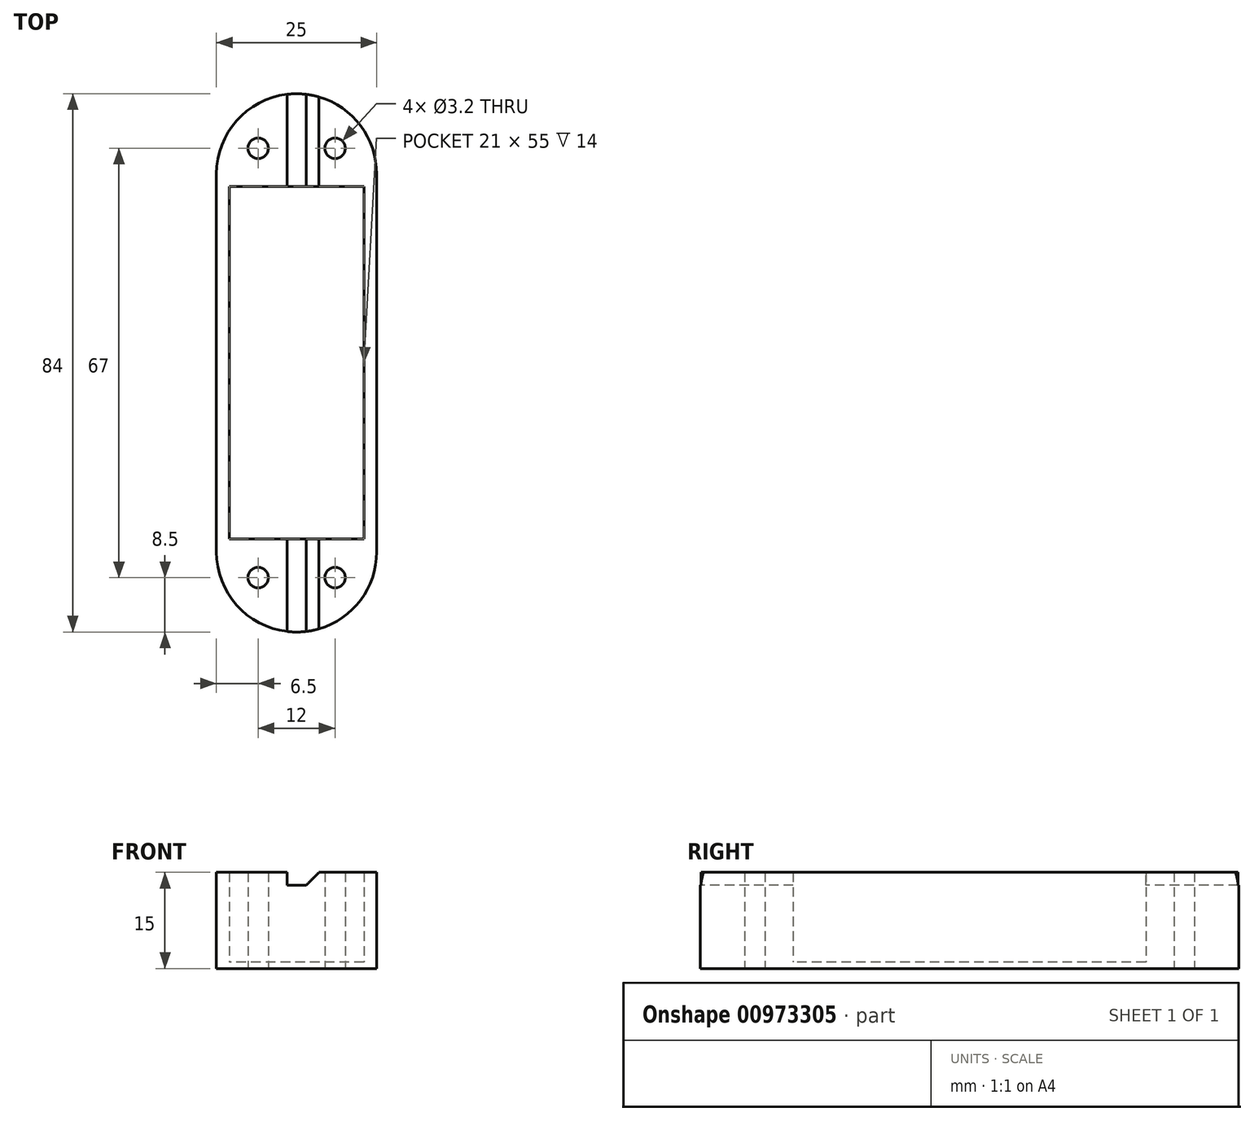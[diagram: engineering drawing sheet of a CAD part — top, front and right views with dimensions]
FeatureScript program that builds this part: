
annotation { "Feature Type Name" : "Feature", "Feature Type Description" : "" }
export const myFeature = defineFeature(function(context is Context, id is Id, definition is map)
    precondition{}
    {
        {
            var Q0;
            Q0=qCreatedBy(makeId("Top.planeOp"),FACE);
            var sketch = newSketch(context, id + "F0", { "sketchPlane" : qUnion([Q0])});
            skLineSegment(sketch, "E0.bottom", {"start": v(10.5, 27.5) * mm, "end": v(-10.5, 27.5) * mm});
            skLineSegment(sketch, "E0.top", {"start": v(10.5, -27.5) * mm, "end": v(-10.5, -27.5) * mm});
            skLineSegment(sketch, "E0.left", {"start": v(10.5, 27.5) * mm, "end": v(10.5, -27.5) * mm});
            skLineSegment(sketch, "E0.right", {"start": v(-10.5, 27.5) * mm, "end": v(-10.5, -27.5) * mm});
            skPoint(sketch, "E0.middle", {"position": v(0, 0) * mm});
            skLineSegment(sketch, "E1.left", {"start": v(12.5, 29.5) * mm, "end": v(12.5, -29.5) * mm});
            skLineSegment(sketch, "E1.right", {"start": v(-12.5, 29.5) * mm, "end": v(-12.5, -29.5) * mm});
            skArc(sketch, "E2", {"start": v(12.5, 29.5) * mm, "mid": v(0, 42) * mm, "end": v(-12.5, 29.5) * mm});
            skArc(sketch, "E3.MirrorCS", {"start": v(12.5, -29.5) * mm, "mid": v(0, -42) * mm, "end": v(-12.5, -29.5) * mm});
            skCircle(sketch, "E4", {"center": v(-6, 33.5) * mm, "radius": 1.6 * mm});
            skCircle(sketch, "E5.MirrorC", {"center": v(6, 33.5) * mm, "radius": 1.6 * mm});
            skCircle(sketch, "E6.MirrorC", {"center": v(-6, -33.5) * mm, "radius": 1.6 * mm});
            skCircle(sketch, "E7.MirrorC", {"center": v(6, -33.5) * mm, "radius": 1.6 * mm});
            skSolve(sketch);
        }
        {
            var Q0;
            Q0=makeQuery(id+"F0.imprint","IMPRINT",FACE,{"disambiguationData":[TD([[makeQuery(id+"F0.imprint","IMPRINT",EDGE,{"derivedFrom":sQuery(id+"F0.wireOp",EDGE,"E0.bottom")}),-1.0]])]});
            extrude(context, id + "F1", {"entities" : qUnion([Q0]), "depth" : 15 * mm, "offsetDistance" : 25 * mm});
        }
        {
            var Q0;
            Q0=qCreatedBy(makeId("Top.planeOp"),FACE);
            var sketch = newSketch(context, id + "F2", { "sketchPlane" : qUnion([Q0])});
            skLineSegment(sketch, "E8.bottom", {"start": v(11.31, -28.6) * mm, "end": v(-11.31, -28.6) * mm});
            skLineSegment(sketch, "E8.top", {"start": v(11.31, 28.6) * mm, "end": v(-11.31, 28.6) * mm});
            skLineSegment(sketch, "E8.left", {"start": v(11.31, -28.6) * mm, "end": v(11.31, 28.6) * mm});
            skLineSegment(sketch, "E8.right", {"start": v(-11.31, -28.6) * mm, "end": v(-11.31, 28.6) * mm});
            skPoint(sketch, "E8.middle", {"position": v(0, 0) * mm});
            skSolve(sketch);
        }
        {
            var Q0;
            Q0=makeQuery(id+"F2.imprint","IMPRINT",FACE,{"disambiguationData":[TD([[makeQuery(id+"F2.imprint","IMPRINT",EDGE,{"derivedFrom":sQuery(id+"F2.wireOp",EDGE,"E8.bottom")}),-1.0]])]});
            extrude(context, id + "F3", {"entities" : qUnion([Q0]), "operationType" : NewBodyOperationType.ADD, "depth" : 1 * mm, "offsetDistance" : 25 * mm});
        }
        {
            var Q0;
            Q0=makeQuery(id+"F1.opExtrude","CAP_FACE",FACE,{"disambiguationData":[OSD([sQuery(id+"F0.wireOp",EDGE,"E0.bottom"),sQuery(id+"F0.wireOp",EDGE,"E0.top"),sQuery(id+"F0.wireOp",EDGE,"E0.left"),sQuery(id+"F0.wireOp",EDGE,"E0.right"),sQuery(id+"F0.wireOp",EDGE,"E1.left"),sQuery(id+"F0.wireOp",EDGE,"E1.right"),sQuery(id+"F0.wireOp",EDGE,"E2"),sQuery(id+"F0.wireOp",EDGE,"E3.MirrorCS"),sQuery(id+"F0.wireOp",EDGE,"E4"),sQuery(id+"F0.wireOp",EDGE,"E5.MirrorC"),sQuery(id+"F0.wireOp",EDGE,"E6.MirrorC"),sQuery(id+"F0.wireOp",EDGE,"E7.MirrorC")])],"isStart":false});
            var sketch = newSketch(context, id + "F4", { "sketchPlane" : qUnion([Q0])});
            skLineSegment(sketch, "E9.bottom", {"start": v(-1.5, 43.23) * mm, "end": v(1.5, 43.23) * mm});
            skLineSegment(sketch, "E9.top", {"start": v(-1.5, -43.23) * mm, "end": v(1.5, -43.23) * mm});
            skLineSegment(sketch, "E9.left", {"start": v(-1.5, 43.23) * mm, "end": v(-1.5, -43.23) * mm});
            skLineSegment(sketch, "E9.right", {"start": v(1.5, 43.23) * mm, "end": v(1.5, -43.23) * mm});
            skPoint(sketch, "E9.middle", {"position": v(0, 0) * mm});
            skSolve(sketch);
        }
        {
            var Q0;
            {var subQ0=sQuery(id+"F4.wireOp",EDGE,"E9.left");var subQ1=makeQuery(id+"F1.opExtrude","CAP_EDGE",EDGE,{"disambiguationData":[OSD([sQuery(id+"F0.wireOp",EDGE,"E2")])],"isStart":false});var subQ2=makeQuery(id+"F4.imprint","INTERSECT",VERTEX,{"derivedFrom":[subQ1,subQ0]});Q0=makeQuery(id+"F4.imprint","IMPRINT",FACE,{"disambiguationData":[TD([[makeQuery(id+"F4.imprint","IMPRINT",EDGE,{"disambiguationData":[TD([[subQ2,-1.0]])],"derivedFrom":subQ0}),1.0]])]});}
            var Q1;
            {var subQ0=sQuery(id+"F4.wireOp",EDGE,"E9.left");var subQ1=makeQuery(id+"F1.opExtrude","CAP_EDGE",EDGE,{"disambiguationData":[OSD([sQuery(id+"F0.wireOp",EDGE,"E3.MirrorCS")])],"isStart":false});var subQ2=makeQuery(id+"F4.imprint","INTERSECT",VERTEX,{"derivedFrom":[subQ1,subQ0]});Q1=makeQuery(id+"F4.imprint","IMPRINT",FACE,{"disambiguationData":[TD([[makeQuery(id+"F4.imprint","IMPRINT",EDGE,{"disambiguationData":[TD([[subQ2,1.0]])],"derivedFrom":subQ0}),1.0]])]});}
            extrude(context, id + "F5", {"entities" : qUnion([Q0, Q1]), "operationType" : NewBodyOperationType.REMOVE, "oppositeDirection" : true, "depth" : 2 * mm, "offsetDistance" : 25 * mm});
        }
        {
            var Q0;
            {var subQ0=sQuery(id+"F4.wireOp",EDGE,"E9.left");Q0=makeQuery(id+"F5.boolean.opBoolean","COPY",EDGE,{"derivedFrom":makeQuery(id+"F5.opExtrude","CAP_EDGE",EDGE,{"disambiguationData":[OSD([subQ0]),TDD([makeQuery(id+"F4.imprint","IMPRINT",EDGE,{"disambiguationData":[TD([[makeQuery(id+"F4.imprint","INTERSECT",VERTEX,{"derivedFrom":[makeQuery(id+"F1.opExtrude","CAP_EDGE",EDGE,{"disambiguationData":[OSD([sQuery(id+"F0.wireOp",EDGE,"E2")])],"isStart":false}),subQ0]}),-1.0]])],"derivedFrom":subQ0})])],"isStart":true})});}
            var Q1;
            {var subQ0=sQuery(id+"F4.wireOp",EDGE,"E9.right");Q1=makeQuery(id+"F5.boolean.opBoolean","COPY",EDGE,{"derivedFrom":makeQuery(id+"F5.opExtrude","CAP_EDGE",EDGE,{"disambiguationData":[OSD([subQ0]),TDD([makeQuery(id+"F4.imprint","IMPRINT",EDGE,{"disambiguationData":[TD([[makeQuery(id+"F4.imprint","INTERSECT",VERTEX,{"derivedFrom":[makeQuery(id+"F1.opExtrude","CAP_EDGE",EDGE,{"disambiguationData":[OSD([sQuery(id+"F0.wireOp",EDGE,"E2")])],"isStart":false}),subQ0]}),-1.0]])],"derivedFrom":subQ0})])],"isStart":true})});}
            var Q2;
            {var subQ0=sQuery(id+"F4.wireOp",EDGE,"E9.right");Q2=makeQuery(id+"F5.boolean.opBoolean","COPY",EDGE,{"derivedFrom":makeQuery(id+"F5.opExtrude","CAP_EDGE",EDGE,{"disambiguationData":[OSD([subQ0]),TDD([makeQuery(id+"F4.imprint","IMPRINT",EDGE,{"disambiguationData":[TD([[makeQuery(id+"F4.imprint","INTERSECT",VERTEX,{"derivedFrom":[makeQuery(id+"F1.opExtrude","CAP_EDGE",EDGE,{"disambiguationData":[OSD([sQuery(id+"F0.wireOp",EDGE,"E3.MirrorCS")])],"isStart":false}),subQ0]}),1.0]])],"derivedFrom":subQ0})])],"isStart":true})});}
            var Q3;
            {var subQ0=sQuery(id+"F4.wireOp",EDGE,"E9.left");Q3=makeQuery(id+"F5.boolean.opBoolean","COPY",EDGE,{"derivedFrom":makeQuery(id+"F5.opExtrude","CAP_EDGE",EDGE,{"disambiguationData":[OSD([subQ0]),TDD([makeQuery(id+"F4.imprint","IMPRINT",EDGE,{"disambiguationData":[TD([[makeQuery(id+"F4.imprint","INTERSECT",VERTEX,{"derivedFrom":[makeQuery(id+"F1.opExtrude","CAP_EDGE",EDGE,{"disambiguationData":[OSD([sQuery(id+"F0.wireOp",EDGE,"E3.MirrorCS")])],"isStart":false}),subQ0]}),1.0]])],"derivedFrom":subQ0})])],"isStart":true})});}
            chamfer(context, id + "F6", {"entities" : qUnion([Q0, Q1, Q2, Q3]), "width" : 2 * mm, "tangentPropagation" : true});
        }
    });
